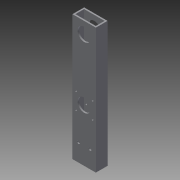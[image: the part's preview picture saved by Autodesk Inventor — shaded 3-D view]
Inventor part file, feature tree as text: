
AUTODESK INVENTOR PART (.ipt)
format: ipt  version: 2013 (Build 170138000, 138)  size: 132,608 bytes
history: native  units: in
note: dims shown in document units (in); Inventor stores cm internally (conversion verified against a paired STEP export)
features: extrude x4, sketch x4
ambient origin geometry x8: Origin, YZ Plane, XZ Plane, XY Plane, X Axis, Y Axis, Z Axis, Center Point
bodies: Solid1 (feature_tree)
feature tree (8):
  extrude  "Extrusion1"  Depth=1.0in
  extrude  "Extrusion2"  Depth=0.75in
  extrude  "Extrusion3"  Depth=1.5in
  extrude  "Extrusion4"  Depth=0.5in
  sketch  "Sketch1"  dims[d0=2.0in d1=1.0in]
  sketch  "Sketch2"  dims[d2=1.75in d3=0.75in]
  sketch  "Sketch3"  dims[d4=10.75in d5=0.0in d6=1.5in]
  sketch  "Sketch4"  dims[d7=90.0deg d8=0.5in d9=90.0deg d10=1.0in d11=0.0in d12=0.25in d13=0.25in d14=8.0in d15=0.0in d16=1.0in d17=90.0deg d18=1.125in d19=1.0in d20=0.0in d21=2.0in d22=3.0in d23=2.0in d24=2.0in d25=1.125in d29=0.16in d30=0.16in d31=0.16in d32=0.16in d33=1.0in d34=0.0in d35=1.5in d36=2.2071in d37=2.2071in d38=0.7929in d39=0.7929in]
